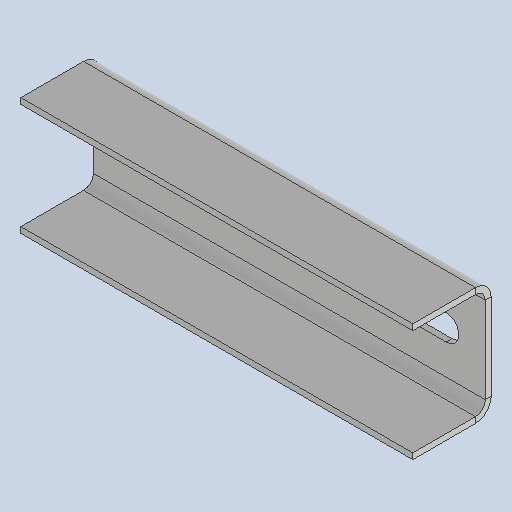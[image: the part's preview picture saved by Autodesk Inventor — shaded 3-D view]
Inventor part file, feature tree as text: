
AUTODESK INVENTOR PART (.ipt)
format: ipt  version: 2025 (Build 290162010, 162A)  size: 286,720 bytes
history: native  units: mm
features: sheet_metal_op x4, other x4, sketch x3
ambient origin geometry x8: Origin, YZ Plane, XZ Plane, XY Plane, X Axis, Y Axis, Z Axis, Center Point
bodies: Body1 (feature_tree)
feature tree (11):
  sheet_metal_op  "Face2"
  sheet_metal_op  "Flange1"
  sketch  "Sketch4"  dims[d36=200.0mm]
  other  "Plate2"
  sketch  "Sketch5"  dims[d37=60.0mm]
  sketch  "Sketch6"  dims[d38=3.0mm d39=160.0mm d40=30.0mm d41=13.0mm d42=3.0mm d43=0.0mm d44=3.0mm d45=1.5mm d46=6.0mm d47=5.0mm d48=40.0mm d49=90.0deg d50=5.0mm d51=12.0mm d52=3.0mm d53=5.0mm d55=60.0mm]
  other  "Plate3"
  sheet_metal_op  "Bend1"
  sheet_metal_op  "Corner1"
  other  "Cut1"
  other  "Definition1"
